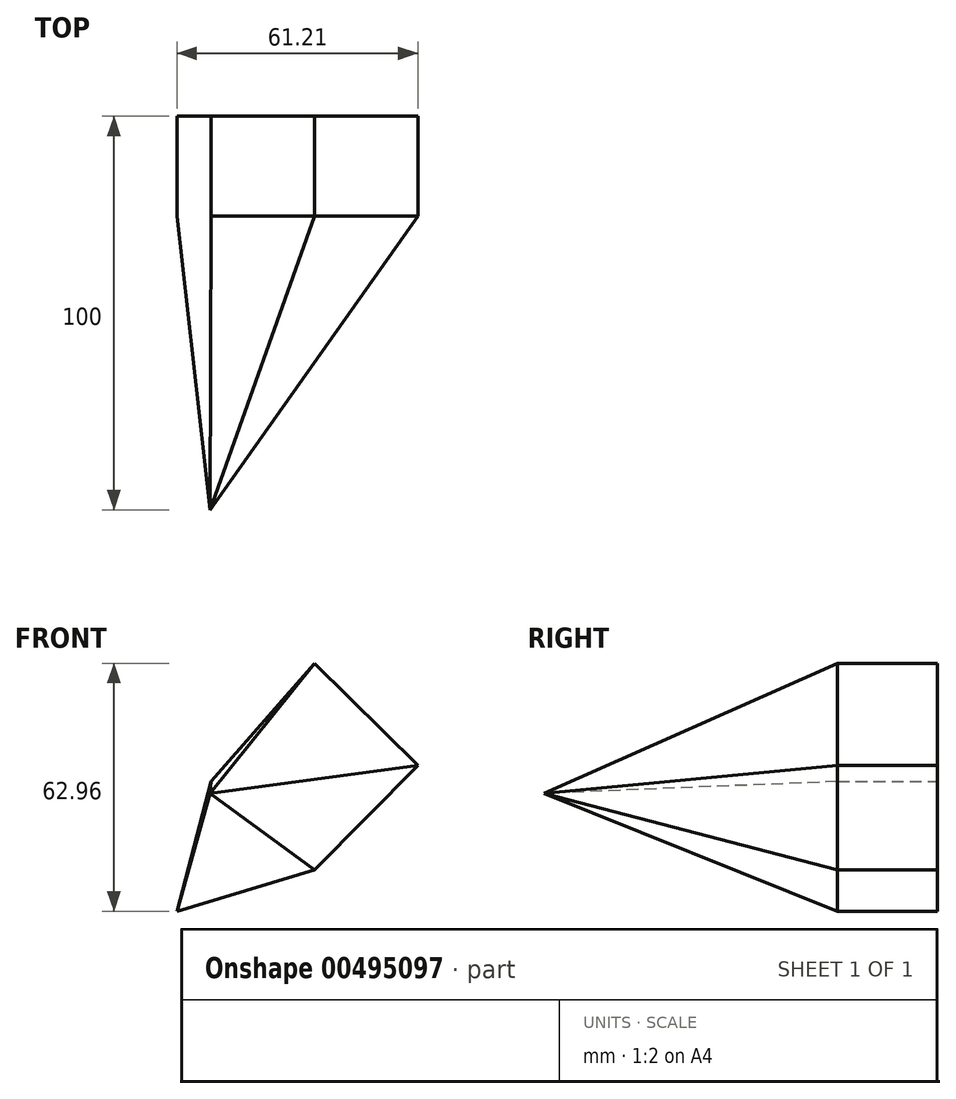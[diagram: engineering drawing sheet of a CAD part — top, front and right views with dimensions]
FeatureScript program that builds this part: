
annotation { "Feature Type Name" : "Feature", "Feature Type Description" : "" }
export const myFeature = defineFeature(function(context is Context, id is Id, definition is map)
    precondition{}
    {
        {
            var Q0;
            Q0=qCreatedBy(makeId("Front.planeOp"),FACE);
            var sketch = newSketch(context, id + "F0", { "sketchPlane" : qUnion([Q0])});
            skLineSegment(sketch, "E0", {"start": v(-38.77, 9.76) * mm, "end": v(-47.51, -23.17) * mm});
            skLineSegment(sketch, "E1", {"start": v(-38.77, 9.76) * mm, "end": v(-12.53, 39.79) * mm});
            skLineSegment(sketch, "E2", {"start": v(-12.53, 39.79) * mm, "end": v(13.7, 13.85) * mm});
            skLineSegment(sketch, "E3", {"start": v(13.7, 13.85) * mm, "end": v(-12.53, -12.68) * mm});
            skLineSegment(sketch, "E4", {"start": v(-12.53, -12.68) * mm, "end": v(-47.51, -23.17) * mm});
            skSolve(sketch);
        }
        {
            var Q0;
            Q0=makeQuery(id+"F0.imprint","IMPRINT",FACE,{"disambiguationData":[TD([[makeQuery(id+"F0.imprint","IMPRINT",EDGE,{"derivedFrom":sQuery(id+"F0.wireOp",EDGE,"E1")}),-1.0]])]});
            var Q1;
            Q1=makeQuery(id+"F0.imprint","IMPRINT",FACE,{"disambiguationData":[TD([[makeQuery(id+"F0.imprint","IMPRINT",EDGE,{"derivedFrom":sQuery(id+"F0.wireOp",EDGE,"E0")}),1.0]])]});
            extrude(context, id + "F1", {"entities" : qUnion([Q0, Q1]), "depth" : 25.4 * mm});
        }
        {
            var Q0;
            Q0=qCreatedBy(makeId("Front.planeOp"),FACE);
            cPlane(context, id + "F2", {"entities" : qUnion([Q0]), "cplaneType" : CPlaneType.OFFSET, "offset" : 100 * mm, "width" : 152.4 * mm, "height" : 152.4 * mm});
        }
        {
            var Q0;
            Q0=qCreatedBy(id+"F2.planeOp",FACE);
            var sketch = newSketch(context, id + "F3", { "sketchPlane" : qUnion([Q0])});
            skPoint(sketch, "E5", {"position": v(-39.08, 6.77) * mm});
            skSolve(sketch);
        }
        {
            var Q1;
            Q1=makeQuery(id+"F1.opExtrude","CAP_FACE",FACE,{"disambiguationData":[OSD([sQuery(id+"F0.wireOp",EDGE,"E0"),sQuery(id+"F0.wireOp",EDGE,"E1"),sQuery(id+"F0.wireOp",EDGE,"E2"),sQuery(id+"F0.wireOp",EDGE,"E3"),sQuery(id+"F0.wireOp",EDGE,"E4")])],"isStart":false});
            var Q2;
            Q2=sQuery(id+"F3.wireOp",VERTEX,"E5");
            loft(context, id + "F4", {"operationType" : NewBodyOperationType.ADD, "sheetProfilesArray" : [{ "sheetProfileEntities" : qUnion([Q1]) }, { "sheetProfileEntities" : qUnion([Q2]) }]});
        }
    });
